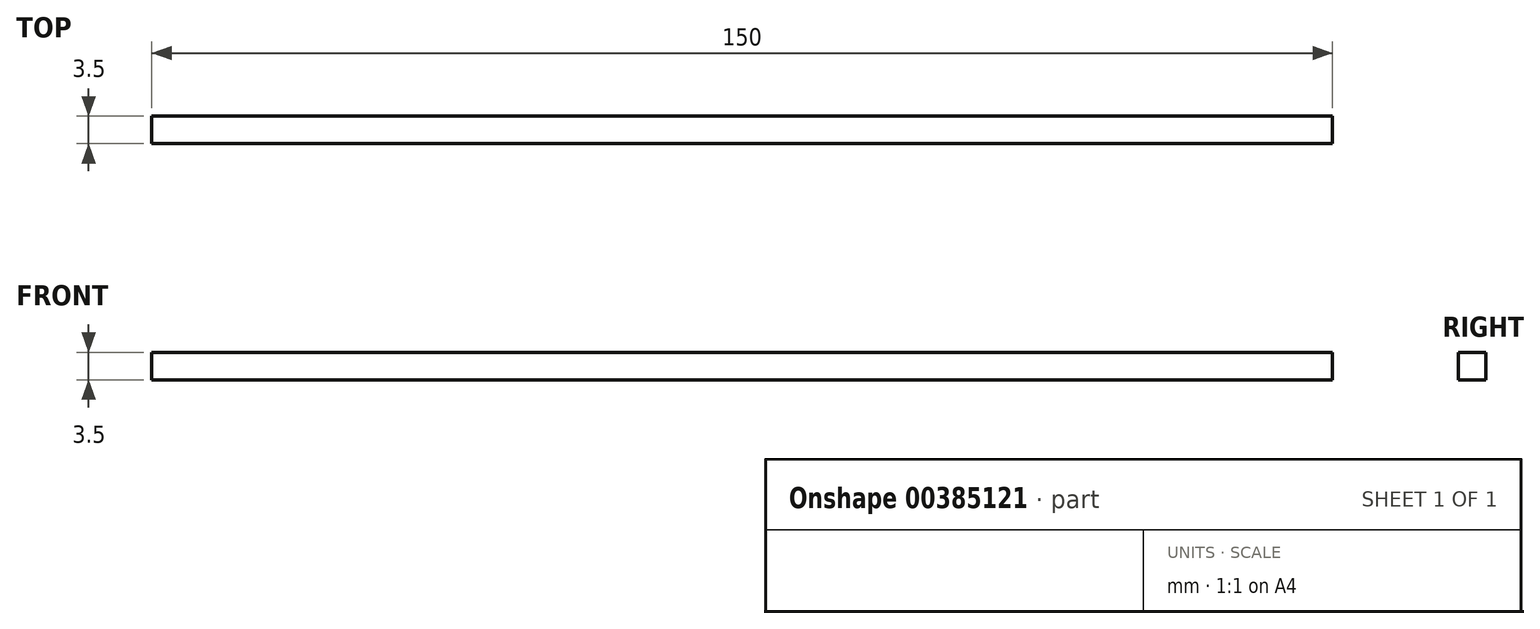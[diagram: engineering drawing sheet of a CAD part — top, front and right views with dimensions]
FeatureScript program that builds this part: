
annotation { "Feature Type Name" : "Feature", "Feature Type Description" : "" }
export const myFeature = defineFeature(function(context is Context, id is Id, definition is map)
    precondition{}
    {
        {
            var Q0;
            Q0=qCreatedBy(makeId("Top.planeOp"),FACE);
            var sketch = newSketch(context, id + "F0", { "sketchPlane" : qUnion([Q0])});
            skLineSegment(sketch, "E0.bottom", {"start": v(0, 0) * mm, "end": v(150, 0) * mm});
            skLineSegment(sketch, "E0.top", {"start": v(0, 3.5) * mm, "end": v(150, 3.5) * mm});
            skLineSegment(sketch, "E0.left", {"start": v(0, 0) * mm, "end": v(0, 3.5) * mm});
            skLineSegment(sketch, "E0.right", {"start": v(150, 0) * mm, "end": v(150, 3.5) * mm});
            skSolve(sketch);
        }
        {
            var Q0;
            Q0=makeQuery(id+"F0.imprint","IMPRINT",FACE,{"disambiguationData":[TD([[makeQuery(id+"F0.imprint","IMPRINT",EDGE,{"derivedFrom":sQuery(id+"F0.wireOp",EDGE,"E0.bottom")}),1.0]])]});
            extrude(context, id + "F1", {"entities" : qUnion([Q0]), "depth" : 3.5 * mm});
        }
    });
